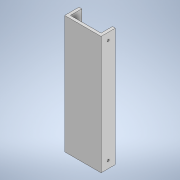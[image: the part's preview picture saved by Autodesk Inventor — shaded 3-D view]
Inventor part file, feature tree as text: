
AUTODESK INVENTOR PART (.ipt)
format: ipt  version: 2020 (Build 240168000, 168)  size: 137,216 bytes
history: native  units: mm
features: sketch x3, extrude x2, other x1, hole x1, mirror x1
ambient origin geometry x8: Origin, YZ Plane, XZ Plane, XY Plane, X Axis, Y Axis, Z Axis, Center Point
bodies: Body1 (feature_tree)
feature tree (8):
  other  "Твердое тело1"
  extrude  "Выдавливание1"  Depth=25.5mm
  extrude  "Выдавливание3"  Depth=10.0mm
  hole  "Отверстие1"  [1 undecoded]
  mirror  "Зеркальное отражение1"
  sketch  "Эскиз1"
  sketch  "Эскиз2"
  sketch  "Эскиз3"
note: 1 required parameter value undecoded (feature->parameter linkage not recoverable at this tier; creation-order binding heuristic only, values carry confidence <= 0.55)
